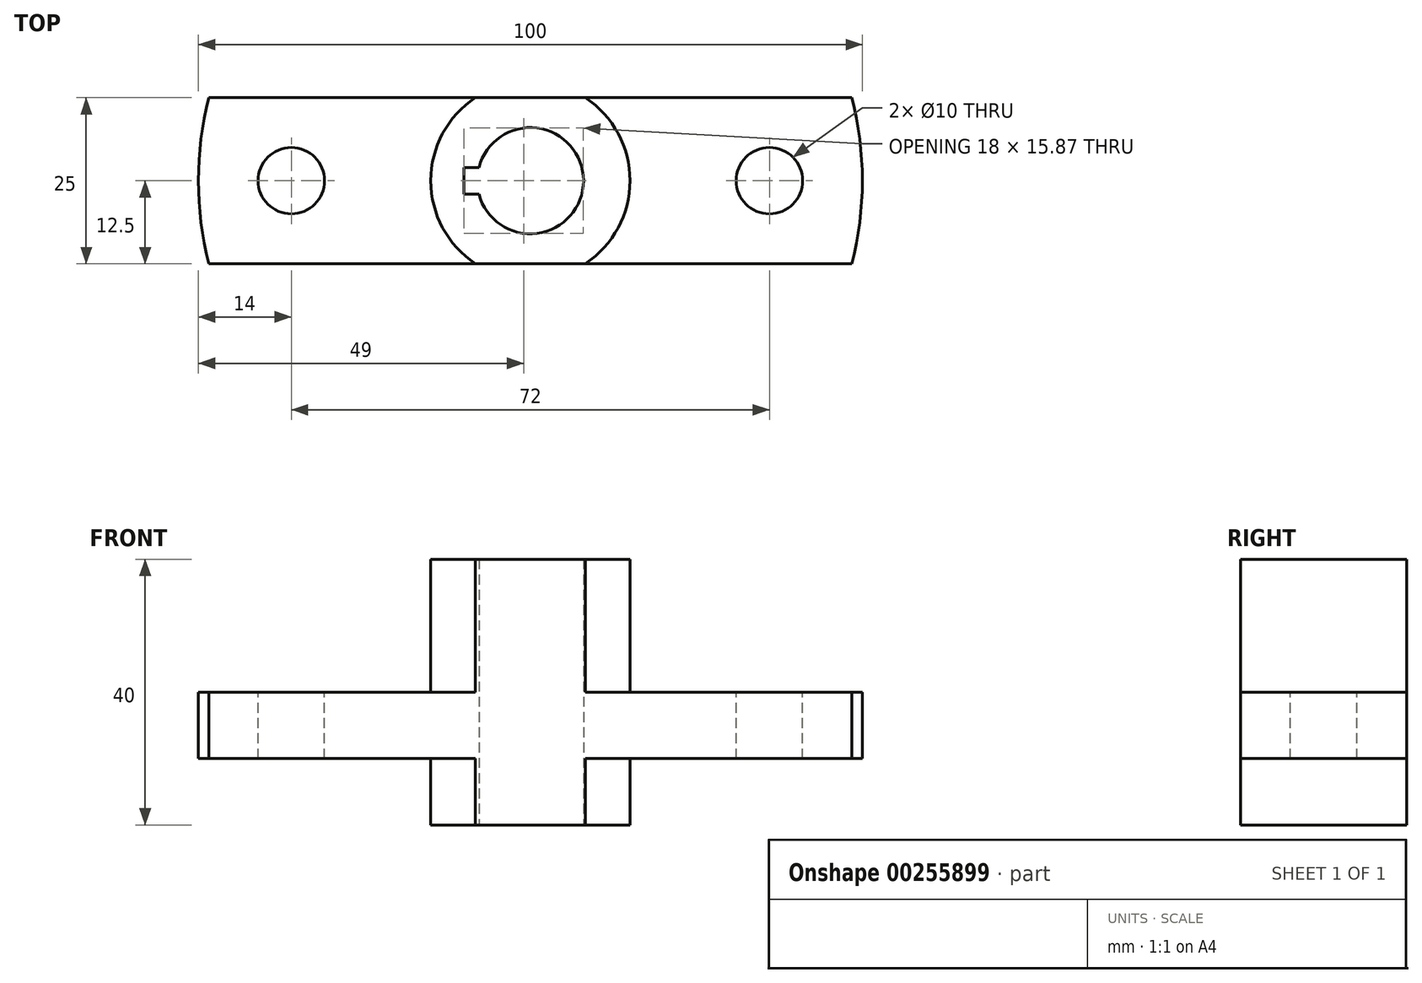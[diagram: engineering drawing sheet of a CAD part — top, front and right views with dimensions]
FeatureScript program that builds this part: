
annotation { "Feature Type Name" : "Feature", "Feature Type Description" : "" }
export const myFeature = defineFeature(function(context is Context, id is Id, definition is map)
    precondition{}
    {
        {
            var Q0;
            Q0=qCreatedBy(makeId("Top.planeOp"),FACE);
            var sketch = newSketch(context, id + "F0", { "sketchPlane" : qUnion([Q0])});
            skArc(sketch, "E0", {"start": v(0, -8) * mm, "mid": v(8, 0) * mm, "end": v(0, 8) * mm});
            skArc(sketch, "E1", {"start": v(8.3, -12.5) * mm, "mid": v(15, 0) * mm, "end": v(8.3, 12.5) * mm});
            skArc(sketch, "E2", {"start": v(48.41, -12.5) * mm, "mid": v(50, 0) * mm, "end": v(48.41, 12.5) * mm});
            skLineSegment(sketch, "E3.bottom", {"start": v(48.41, 12.5) * mm, "end": v(0, 12.5) * mm});
            skLineSegment(sketch, "E3.top", {"start": v(48.41, -12.5) * mm, "end": v(0, -12.5) * mm});
            skPoint(sketch, "E3.middle", {"position": v(26.6, 0) * mm});
            skCircle(sketch, "E4", {"center": v(36, 0) * mm, "radius": 5 * mm});
            skLineSegment(sketch, "E5", {"start": v(0, 21) * mm, "end": v(0, -19.54) * mm});
            skPoint(sketch, "E6.orphan", {"position": v(-7.4, 12.5) * mm});
            skPoint(sketch, "E7.orphan", {"position": v(-7.4, -12.5) * mm});
            skPoint(sketch, "E8.orphan", {"position": v(60.6, 12.5) * mm});
            skPoint(sketch, "E9.orphan", {"position": v(60.6, -12.5) * mm});
            skSolve(sketch);
        }
        {
            var Q0;
            {var subQ6=sQuery(id+"F0.wireOp",EDGE,"E0");Q0=makeQuery(id+"F0.imprint","IMPRINT",FACE,{"disambiguationData":[TD([[makeQuery(id+"F0.imprint","IMPRINT",EDGE,{"derivedFrom":subQ6}),-1.0]])]});}
            extrude(context, id + "F1", {"entities" : qUnion([Q0]), "depth" : 20 * mm, "hasSecondDirection" : true, "secondDirectionOppositeDirection" : true, "secondDirectionDepth" : 20 * mm});
        }
        {
            var Q0;
            {var subQ1=sQuery(id+"F0.wireOp",EDGE,"E1");Q0=makeQuery(id+"F0.imprint","IMPRINT",FACE,{"disambiguationData":[TD([[makeQuery(id+"F0.imprint","IMPRINT",EDGE,{"derivedFrom":subQ1}),-1.0]])]});}
            extrude(context, id + "F2", {"entities" : qUnion([Q0]), "operationType" : NewBodyOperationType.ADD, "oppositeDirection" : true, "depth" : 10 * mm});
        }
        {
            var Q0;
            Q0=makeQuery(id+"F1.opExtrude","SWEPT_BODY",BODY,{"disambiguationData":[OSD([sQuery(id+"F0.wireOp",EDGE,"E0"),sQuery(id+"F0.wireOp",EDGE,"E1"),sQuery(id+"F0.wireOp",EDGE,"E3.bottom"),sQuery(id+"F0.wireOp",EDGE,"E3.top"),sQuery(id+"F0.wireOp",EDGE,"E5")])]});
            var Q1;
            Q1=qCreatedBy(makeId("Right.planeOp"),FACE);
            mirror(context, id + "F3", {"operationType" : NewBodyOperationType.ADD, "entities" : qUnion([Q0]), "mirrorPlane" : qUnion([Q1])});
        }
        {
            var Q0;
            Q0=qCreatedBy(makeId("Top.planeOp"),FACE);
            cPlane(context, id + "F4", {"entities" : qUnion([Q0]), "cplaneType" : CPlaneType.OFFSET, "offset" : 25 * mm, "width" : 150 * mm, "height" : 150 * mm});
        }
        {
            var Q0;
            Q0=qCreatedBy(id+"F4.planeOp",FACE);
            var sketch = newSketch(context, id + "F5", { "sketchPlane" : qUnion([Q0])});
            skLineSegment(sketch, "E10.bottom", {"start": v(-5.76, 2) * mm, "end": v(-10, 2) * mm});
            skLineSegment(sketch, "E10.top", {"start": v(-5.76, -2) * mm, "end": v(-10, -2) * mm});
            skLineSegment(sketch, "E10.left", {"start": v(-5.76, 2) * mm, "end": v(-5.76, -2) * mm});
            skLineSegment(sketch, "E10.right", {"start": v(-10, 2) * mm, "end": v(-10, -2) * mm});
            skPoint(sketch, "E10.middle", {"position": v(-7.88, 0) * mm});
            skSolve(sketch);
        }
        {
            var Q0;
            Q0=makeQuery(id+"F5.imprint","IMPRINT",FACE,{"disambiguationData":[TD([[makeQuery(id+"F5.imprint","IMPRINT",EDGE,{"derivedFrom":sQuery(id+"F5.wireOp",EDGE,"E10.bottom")}),1.0]])]});
            extrude(context, id + "F6", {"entities" : qUnion([Q0]), "operationType" : NewBodyOperationType.REMOVE, "endBound" : BoundingType.THROUGH_ALL, "oppositeDirection" : true, "depth" : 25 * mm});
        }
    });
